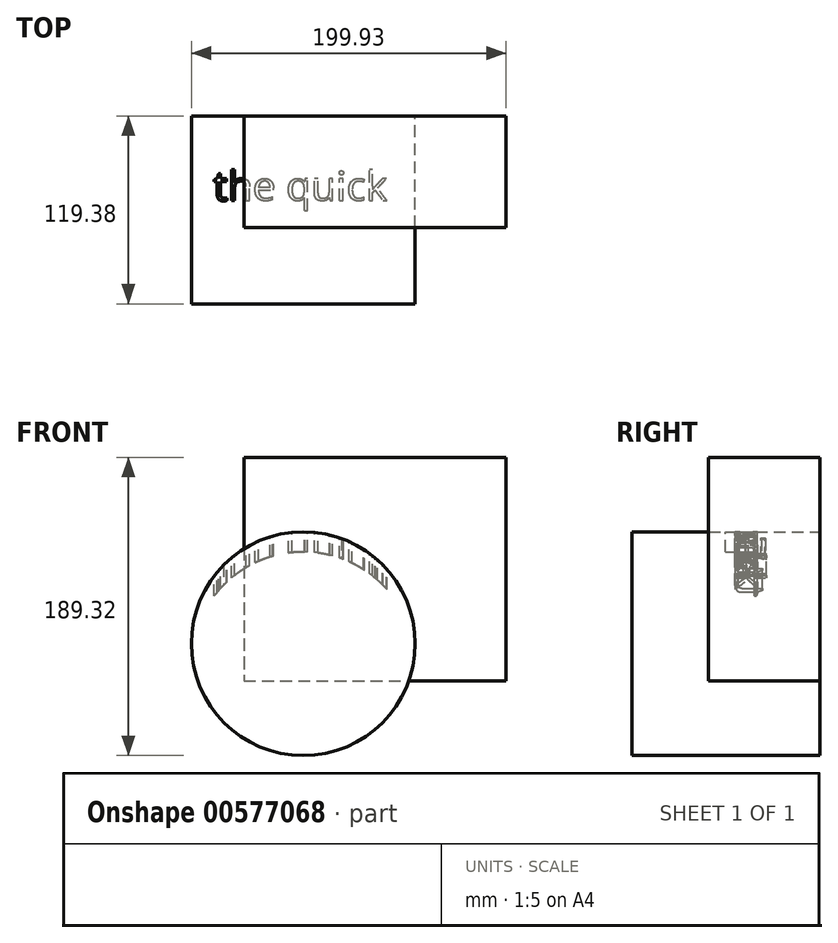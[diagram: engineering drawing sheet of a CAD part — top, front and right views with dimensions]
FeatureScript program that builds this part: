
annotation { "Feature Type Name" : "Feature", "Feature Type Description" : "" }
export const myFeature = defineFeature(function(context is Context, id is Id, definition is map)
    precondition{}
    {
        {
            var Q0;
            Q0=qCreatedBy(makeId("Front.planeOp"),FACE);
            var sketch = newSketch(context, id + "F0", { "sketchPlane" : qUnion([Q0])});
            skCircle(sketch, "E0", {"center": v(0, 0) * mm, "radius": 71.05 * mm});
            skLineSegment(sketch, "E1.bottom", {"start": v(-37.64, 118.27) * mm, "end": v(128.88, 118.27) * mm});
            skLineSegment(sketch, "E1.top", {"start": v(-37.64, -23.55) * mm, "end": v(128.88, -23.55) * mm});
            skLineSegment(sketch, "E1.left", {"start": v(-37.64, 118.27) * mm, "end": v(-37.64, -23.55) * mm});
            skLineSegment(sketch, "E1.right", {"start": v(128.88, 118.27) * mm, "end": v(128.88, -23.55) * mm});
            skSolve(sketch);
        }
        {
            var Q0;
            Q0=makeQuery(id+"F0.imprint","IMPRINT",FACE,{"disambiguationData":[TD([[makeQuery(id+"F0.imprint","IMPRINT",EDGE,{"derivedFrom":sQuery(id+"F0.wireOp",EDGE,"E0")}),1.0]])]});
            extrude(context, id + "F1", {"entities" : qUnion([Q0]), "depth" : 119.38 * mm, "offsetDistance" : 25.4 * mm});
        }
        {
            var Q0;
            {var subQ0=sQuery(id+"F0.wireOp",EDGE,"E1.top");var subQ1=sQuery(id+"F0.wireOp",EDGE,"E0");var subQ2=makeQuery(id+"F0.imprint","INTERSECT",VERTEX,{"derivedFrom":[subQ1,subQ0]});Q0=makeQuery(id+"F0.imprint","IMPRINT",FACE,{"disambiguationData":[TD([[makeQuery(id+"F0.imprint","IMPRINT",EDGE,{"disambiguationData":[TD([[subQ2,-1.0]])],"derivedFrom":subQ1}),1.0]])]});}
            var Q1;
            {var subQ1=sQuery(id+"F0.wireOp",EDGE,"E1.bottom");Q1=makeQuery(id+"F0.imprint","IMPRINT",FACE,{"disambiguationData":[TD([[makeQuery(id+"F0.imprint","IMPRINT",EDGE,{"derivedFrom":subQ1}),-1.0]])]});}
            extrude(context, id + "F2", {"entities" : qUnion([Q0, Q1]), "depth" : 70.87 * mm, "offsetDistance" : 25.4 * mm});
        }
        {
            var Q0;
            Q0=qCreatedBy(makeId("Top.planeOp"),FACE);
            cPlane(context, id + "F3", {"entities" : qUnion([Q0]), "cplaneType" : CPlaneType.OFFSET, "offset" : 170.18 * mm, "width" : 152.4 * mm, "height" : 152.4 * mm});
        }
        {
            var Q0;
            Q0=qCreatedBy(id+"F3.planeOp",FACE);
            var sketch = newSketch(context, id + "F4", { "sketchPlane" : qUnion([Q0])});
            skText(sketch, "E2", { "text": "the quick", "fontName": "OpenSans-Regular.ttf"});
            const initialGuessF4  = {"E2": [-0.05704, -0.05374, 1, 0, 0.01863]};
            skSetInitialGuess(sketch, initialGuessF4);
            skSolve(sketch);
        }
        {
            var Q0;
            Q0 = qSketchRegion(id + "F4", true);
            var Q1;
            Q1=makeQuery(id+"F1.opExtrude","SWEPT_FACE",FACE,{"disambiguationData":[OSD([sQuery(id+"F0.wireOp",EDGE,"E0")])]});
            var Q2;
            Q2=makeQuery(id+"F1.opExtrude","SWEPT_BODY",BODY,{"disambiguationData":[OSD([sQuery(id+"F0.wireOp",EDGE,"E0")])]});
            extrude(context, id + "F5", {"entities" : qUnion([Q0]), "endBound" : BoundingType.UP_TO_SURFACE, "oppositeDirection" : true, "depth" : 25.4 * mm, "endBoundEntityFace" : qUnion([Q1]), "hasOffset" : true, "offsetDistance" : 12.7 * mm, "offsetOppositeDirection" : true, "hasSecondDirection" : true, "secondDirectionBound" : SecondDirectionBoundingType.UP_TO_BODY, "secondDirectionOppositeDirection" : true, "secondDirectionDepth" : 25.4 * mm, "secondDirectionBoundEntityBody" : qUnion([Q2])});
        }
        {
            var Q0;
            Q0=makeQuery(id+"F5.opExtrude","SWEPT_BODY",BODY,{"disambiguationData":[OSD([sQuery(id+"F4.wireOp",EDGE,"E2.sketch_text.stroke-0"),sQuery(id+"F4.wireOp",EDGE,"E2.sketch_text.stroke-1"),sQuery(id+"F4.wireOp",EDGE,"E2.sketch_text.stroke-2"),sQuery(id+"F4.wireOp",EDGE,"E2.sketch_text.stroke-3"),sQuery(id+"F4.wireOp",EDGE,"E2.sketch_text.stroke-4"),sQuery(id+"F4.wireOp",EDGE,"E2.sketch_text.stroke-5"),sQuery(id+"F4.wireOp",EDGE,"E2.sketch_text.stroke-6"),sQuery(id+"F4.wireOp",EDGE,"E2.sketch_text.stroke-7"),sQuery(id+"F4.wireOp",EDGE,"E2.sketch_text.stroke-8"),sQuery(id+"F4.wireOp",EDGE,"E2.sketch_text.stroke-9"),sQuery(id+"F4.wireOp",EDGE,"E2.sketch_text.stroke-10"),sQuery(id+"F4.wireOp",EDGE,"E2.sketch_text.stroke-11"),sQuery(id+"F4.wireOp",EDGE,"E2.sketch_text.stroke-12"),sQuery(id+"F4.wireOp",EDGE,"E2.sketch_text.stroke-13"),sQuery(id+"F4.wireOp",EDGE,"E2.sketch_text.stroke-14"),sQuery(id+"F4.wireOp",EDGE,"E2.sketch_text.stroke-15"),sQuery(id+"F4.wireOp",EDGE,"E2.sketch_text.stroke-16"),sQuery(id+"F4.wireOp",EDGE,"E2.sketch_text.stroke-17"),sQuery(id+"F4.wireOp",EDGE,"E2.sketch_text.stroke-18")])]});
            var Q1;
            Q1=makeQuery(id+"F5.opExtrude","SWEPT_BODY",BODY,{"disambiguationData":[OSD([sQuery(id+"F4.wireOp",EDGE,"E2.sketch_text.stroke-19"),sQuery(id+"F4.wireOp",EDGE,"E2.sketch_text.stroke-20"),sQuery(id+"F4.wireOp",EDGE,"E2.sketch_text.stroke-21"),sQuery(id+"F4.wireOp",EDGE,"E2.sketch_text.stroke-22"),sQuery(id+"F4.wireOp",EDGE,"E2.sketch_text.stroke-23"),sQuery(id+"F4.wireOp",EDGE,"E2.sketch_text.stroke-24"),sQuery(id+"F4.wireOp",EDGE,"E2.sketch_text.stroke-25"),sQuery(id+"F4.wireOp",EDGE,"E2.sketch_text.stroke-26"),sQuery(id+"F4.wireOp",EDGE,"E2.sketch_text.stroke-27"),sQuery(id+"F4.wireOp",EDGE,"E2.sketch_text.stroke-28"),sQuery(id+"F4.wireOp",EDGE,"E2.sketch_text.stroke-29"),sQuery(id+"F4.wireOp",EDGE,"E2.sketch_text.stroke-30"),sQuery(id+"F4.wireOp",EDGE,"E2.sketch_text.stroke-31"),sQuery(id+"F4.wireOp",EDGE,"E2.sketch_text.stroke-32"),sQuery(id+"F4.wireOp",EDGE,"E2.sketch_text.stroke-33"),sQuery(id+"F4.wireOp",EDGE,"E2.sketch_text.stroke-34"),sQuery(id+"F4.wireOp",EDGE,"E2.sketch_text.stroke-35"),sQuery(id+"F4.wireOp",EDGE,"E2.sketch_text.stroke-36")])]});
            var Q2;
            Q2=makeQuery(id+"F5.opExtrude","SWEPT_BODY",BODY,{"disambiguationData":[OSD([sQuery(id+"F4.wireOp",EDGE,"E2.sketch_text.stroke-37"),sQuery(id+"F4.wireOp",EDGE,"E2.sketch_text.stroke-38"),sQuery(id+"F4.wireOp",EDGE,"E2.sketch_text.stroke-39"),sQuery(id+"F4.wireOp",EDGE,"E2.sketch_text.stroke-40"),sQuery(id+"F4.wireOp",EDGE,"E2.sketch_text.stroke-41"),sQuery(id+"F4.wireOp",EDGE,"E2.sketch_text.stroke-42"),sQuery(id+"F4.wireOp",EDGE,"E2.sketch_text.stroke-43"),sQuery(id+"F4.wireOp",EDGE,"E2.sketch_text.stroke-44"),sQuery(id+"F4.wireOp",EDGE,"E2.sketch_text.stroke-45"),sQuery(id+"F4.wireOp",EDGE,"E2.sketch_text.stroke-46"),sQuery(id+"F4.wireOp",EDGE,"E2.sketch_text.stroke-47"),sQuery(id+"F4.wireOp",EDGE,"E2.sketch_text.stroke-48"),sQuery(id+"F4.wireOp",EDGE,"E2.sketch_text.stroke-49"),sQuery(id+"F4.wireOp",EDGE,"E2.sketch_text.stroke-50"),sQuery(id+"F4.wireOp",EDGE,"E2.sketch_text.stroke-51"),sQuery(id+"F4.wireOp",EDGE,"E2.sketch_text.stroke-52"),sQuery(id+"F4.wireOp",EDGE,"E2.sketch_text.stroke-53"),sQuery(id+"F4.wireOp",EDGE,"E2.sketch_text.stroke-54"),sQuery(id+"F4.wireOp",EDGE,"E2.sketch_text.stroke-55")])]});
            var Q3;
            Q3=makeQuery(id+"F5.opExtrude","SWEPT_BODY",BODY,{"disambiguationData":[OSD([sQuery(id+"F4.wireOp",EDGE,"E2.sketch_text.stroke-56"),sQuery(id+"F4.wireOp",EDGE,"E2.sketch_text.stroke-57"),sQuery(id+"F4.wireOp",EDGE,"E2.sketch_text.stroke-58"),sQuery(id+"F4.wireOp",EDGE,"E2.sketch_text.stroke-59"),sQuery(id+"F4.wireOp",EDGE,"E2.sketch_text.stroke-60"),sQuery(id+"F4.wireOp",EDGE,"E2.sketch_text.stroke-61"),sQuery(id+"F4.wireOp",EDGE,"E2.sketch_text.stroke-62"),sQuery(id+"F4.wireOp",EDGE,"E2.sketch_text.stroke-63"),sQuery(id+"F4.wireOp",EDGE,"E2.sketch_text.stroke-64"),sQuery(id+"F4.wireOp",EDGE,"E2.sketch_text.stroke-65"),sQuery(id+"F4.wireOp",EDGE,"E2.sketch_text.stroke-66"),sQuery(id+"F4.wireOp",EDGE,"E2.sketch_text.stroke-67"),sQuery(id+"F4.wireOp",EDGE,"E2.sketch_text.stroke-68"),sQuery(id+"F4.wireOp",EDGE,"E2.sketch_text.stroke-69"),sQuery(id+"F4.wireOp",EDGE,"E2.sketch_text.stroke-70"),sQuery(id+"F4.wireOp",EDGE,"E2.sketch_text.stroke-71"),sQuery(id+"F4.wireOp",EDGE,"E2.sketch_text.stroke-72"),sQuery(id+"F4.wireOp",EDGE,"E2.sketch_text.stroke-73"),sQuery(id+"F4.wireOp",EDGE,"E2.sketch_text.stroke-74"),sQuery(id+"F4.wireOp",EDGE,"E2.sketch_text.stroke-75"),sQuery(id+"F4.wireOp",EDGE,"E2.sketch_text.stroke-76"),sQuery(id+"F4.wireOp",EDGE,"E2.sketch_text.stroke-77"),sQuery(id+"F4.wireOp",EDGE,"E2.sketch_text.stroke-78")])]});
            var Q4;
            Q4=makeQuery(id+"F5.opExtrude","SWEPT_BODY",BODY,{"disambiguationData":[OSD([sQuery(id+"F4.wireOp",EDGE,"E2.sketch_text.stroke-79"),sQuery(id+"F4.wireOp",EDGE,"E2.sketch_text.stroke-80"),sQuery(id+"F4.wireOp",EDGE,"E2.sketch_text.stroke-81"),sQuery(id+"F4.wireOp",EDGE,"E2.sketch_text.stroke-82"),sQuery(id+"F4.wireOp",EDGE,"E2.sketch_text.stroke-83"),sQuery(id+"F4.wireOp",EDGE,"E2.sketch_text.stroke-84"),sQuery(id+"F4.wireOp",EDGE,"E2.sketch_text.stroke-85"),sQuery(id+"F4.wireOp",EDGE,"E2.sketch_text.stroke-86"),sQuery(id+"F4.wireOp",EDGE,"E2.sketch_text.stroke-87"),sQuery(id+"F4.wireOp",EDGE,"E2.sketch_text.stroke-88"),sQuery(id+"F4.wireOp",EDGE,"E2.sketch_text.stroke-89"),sQuery(id+"F4.wireOp",EDGE,"E2.sketch_text.stroke-90"),sQuery(id+"F4.wireOp",EDGE,"E2.sketch_text.stroke-91"),sQuery(id+"F4.wireOp",EDGE,"E2.sketch_text.stroke-92"),sQuery(id+"F4.wireOp",EDGE,"E2.sketch_text.stroke-93"),sQuery(id+"F4.wireOp",EDGE,"E2.sketch_text.stroke-94"),sQuery(id+"F4.wireOp",EDGE,"E2.sketch_text.stroke-95")])]});
            var Q5;
            Q5=makeQuery(id+"F5.opExtrude","SWEPT_BODY",BODY,{"disambiguationData":[OSD([sQuery(id+"F4.wireOp",EDGE,"E2.sketch_text.stroke-96"),sQuery(id+"F4.wireOp",EDGE,"E2.sketch_text.stroke-97"),sQuery(id+"F4.wireOp",EDGE,"E2.sketch_text.stroke-98"),sQuery(id+"F4.wireOp",EDGE,"E2.sketch_text.stroke-99")])]});
            var Q6;
            Q6=makeQuery(id+"F5.opExtrude","SWEPT_BODY",BODY,{"disambiguationData":[OSD([sQuery(id+"F4.wireOp",EDGE,"E2.sketch_text.stroke-100"),sQuery(id+"F4.wireOp",EDGE,"E2.sketch_text.stroke-101"),sQuery(id+"F4.wireOp",EDGE,"E2.sketch_text.stroke-102"),sQuery(id+"F4.wireOp",EDGE,"E2.sketch_text.stroke-103"),sQuery(id+"F4.wireOp",EDGE,"E2.sketch_text.stroke-104"),sQuery(id+"F4.wireOp",EDGE,"E2.sketch_text.stroke-105"),sQuery(id+"F4.wireOp",EDGE,"E2.sketch_text.stroke-106"),sQuery(id+"F4.wireOp",EDGE,"E2.sketch_text.stroke-107")])]});
            var Q7;
            Q7=makeQuery(id+"F5.opExtrude","SWEPT_BODY",BODY,{"disambiguationData":[OSD([sQuery(id+"F4.wireOp",EDGE,"E2.sketch_text.stroke-108"),sQuery(id+"F4.wireOp",EDGE,"E2.sketch_text.stroke-109"),sQuery(id+"F4.wireOp",EDGE,"E2.sketch_text.stroke-110"),sQuery(id+"F4.wireOp",EDGE,"E2.sketch_text.stroke-111"),sQuery(id+"F4.wireOp",EDGE,"E2.sketch_text.stroke-112"),sQuery(id+"F4.wireOp",EDGE,"E2.sketch_text.stroke-113"),sQuery(id+"F4.wireOp",EDGE,"E2.sketch_text.stroke-114"),sQuery(id+"F4.wireOp",EDGE,"E2.sketch_text.stroke-115"),sQuery(id+"F4.wireOp",EDGE,"E2.sketch_text.stroke-116"),sQuery(id+"F4.wireOp",EDGE,"E2.sketch_text.stroke-117"),sQuery(id+"F4.wireOp",EDGE,"E2.sketch_text.stroke-118"),sQuery(id+"F4.wireOp",EDGE,"E2.sketch_text.stroke-119"),sQuery(id+"F4.wireOp",EDGE,"E2.sketch_text.stroke-120"),sQuery(id+"F4.wireOp",EDGE,"E2.sketch_text.stroke-121"),sQuery(id+"F4.wireOp",EDGE,"E2.sketch_text.stroke-122")])]});
            var Q8;
            Q8=makeQuery(id+"F5.opExtrude","SWEPT_BODY",BODY,{"disambiguationData":[OSD([sQuery(id+"F4.wireOp",EDGE,"E2.sketch_text.stroke-123"),sQuery(id+"F4.wireOp",EDGE,"E2.sketch_text.stroke-124"),sQuery(id+"F4.wireOp",EDGE,"E2.sketch_text.stroke-125"),sQuery(id+"F4.wireOp",EDGE,"E2.sketch_text.stroke-126"),sQuery(id+"F4.wireOp",EDGE,"E2.sketch_text.stroke-127"),sQuery(id+"F4.wireOp",EDGE,"E2.sketch_text.stroke-128"),sQuery(id+"F4.wireOp",EDGE,"E2.sketch_text.stroke-129"),sQuery(id+"F4.wireOp",EDGE,"E2.sketch_text.stroke-130"),sQuery(id+"F4.wireOp",EDGE,"E2.sketch_text.stroke-131"),sQuery(id+"F4.wireOp",EDGE,"E2.sketch_text.stroke-132"),sQuery(id+"F4.wireOp",EDGE,"E2.sketch_text.stroke-133"),sQuery(id+"F4.wireOp",EDGE,"E2.sketch_text.stroke-134"),sQuery(id+"F4.wireOp",EDGE,"E2.sketch_text.stroke-135"),sQuery(id+"F4.wireOp",EDGE,"E2.sketch_text.stroke-136"),sQuery(id+"F4.wireOp",EDGE,"E2.sketch_text.stroke-137")])]});
            var Q9;
            Q9=makeQuery(id+"F1.opExtrude","SWEPT_BODY",BODY,{"disambiguationData":[OSD([sQuery(id+"F0.wireOp",EDGE,"E0")])]});
            booleanBodies(context, id + "F6", {"operationType" : BooleanOperationType.SUBTRACTION, "tools" : qUnion([Q0, Q1, Q2, Q3, Q4, Q5, Q6, Q7, Q8]), "targets" : qUnion([Q9]), "keepTools" : true});
        }
    });
